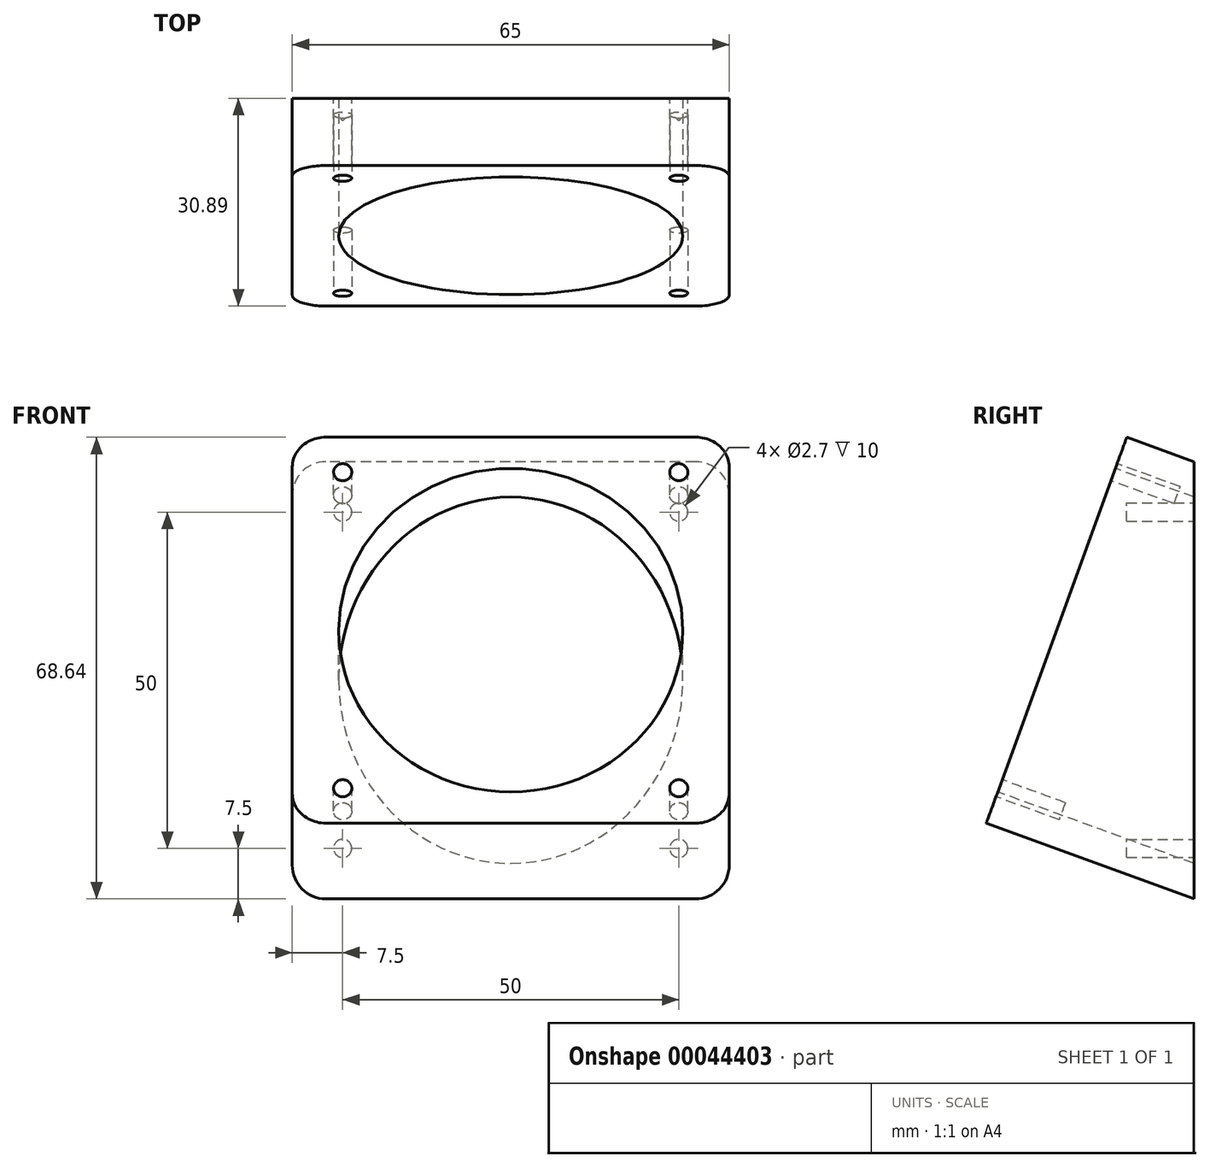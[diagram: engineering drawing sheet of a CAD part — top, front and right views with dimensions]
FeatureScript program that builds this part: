
annotation { "Feature Type Name" : "Feature", "Feature Type Description" : "" }
export const myFeature = defineFeature(function(context is Context, id is Id, definition is map)
    precondition{}
    {
        {
            var Q0;
            Q0=qCreatedBy(makeId("Front.planeOp"),FACE);
            var sketch = newSketch(context, id + "F0", { "sketchPlane" : qUnion([Q0])});
            skLineSegment(sketch, "E0.rect.bottom", {"start": v(27.5, 32.5) * mm, "end": v(-27.5, 32.5) * mm});
            skLineSegment(sketch, "E0.rect.top", {"start": v(27.5, -32.5) * mm, "end": v(-27.5, -32.5) * mm});
            skLineSegment(sketch, "E0.rect.left", {"start": v(32.5, 27.5) * mm, "end": v(32.5, -27.5) * mm});
            skLineSegment(sketch, "E0.rect.right", {"start": v(-32.5, 27.5) * mm, "end": v(-32.5, -27.5) * mm});
            skPoint(sketch, "E0.rect.middle", {"position": v(0, 0) * mm});
            skPoint(sketch, "E1.visualSharp", {"position": v(-32.5, 32.5) * mm});
            skArc(sketch, "E1.filletArc", {"start": v(-27.5, 32.5) * mm, "mid": v(-31.04, 31.04) * mm, "end": v(-32.5, 27.5) * mm});
            skPoint(sketch, "E2.visualSharp", {"position": v(-32.5, -32.5) * mm});
            skArc(sketch, "E2.filletArc", {"start": v(-32.5, -27.5) * mm, "mid": v(-31.04, -31.04) * mm, "end": v(-27.5, -32.5) * mm});
            skPoint(sketch, "E3.visualSharp", {"position": v(32.5, -32.5) * mm});
            skArc(sketch, "E3.filletArc", {"start": v(27.5, -32.5) * mm, "mid": v(31.04, -31.04) * mm, "end": v(32.5, -27.5) * mm});
            skPoint(sketch, "E4.visualSharp", {"position": v(32.5, 32.5) * mm});
            skArc(sketch, "E4.filletArc", {"start": v(32.5, 27.5) * mm, "mid": v(31.04, 31.04) * mm, "end": v(27.5, 32.5) * mm});
            skSolve(sketch);
        }
        {
            var Q0;
            Q0=qCreatedBy(makeId("Front.planeOp"),FACE);
            var sketch = newSketch(context, id + "F1", { "sketchPlane" : qUnion([Q0])});
            skCircle(sketch, "E5", {"center": v(-25, 25) * mm, "radius": 1.35 * mm});
            skCircle(sketch, "E6.MirrorC", {"center": v(25, 25) * mm, "radius": 1.35 * mm});
            skCircle(sketch, "E7.MirrorC", {"center": v(-25, -25) * mm, "radius": 1.35 * mm});
            skCircle(sketch, "E8.MirrorC", {"center": v(25, -25) * mm, "radius": 1.35 * mm});
            skSolve(sketch);
        }
        {
            var Q0;
            Q0=qCreatedBy(makeId("Top.planeOp"),FACE);
            var sketch = newSketch(context, id + "F2", { "sketchPlane" : qUnion([Q0])});
            skLineSegment(sketch, "E9", {"start": v(44.2, -23.15) * mm, "end": v(-58.35, -23.15) * mm, "construction": true});
            skSolve(sketch);
        }
        {
            var Q0;
            Q0=sQuery(id+"F2.wireOp",EDGE,"E9");
            var Q1;
            Q1=qCreatedBy(makeId("Front.planeOp"),FACE);
            cPlane(context, id + "F3", {"entities" : qUnion([Q0, Q1]), "cplaneType" : CPlaneType.LINE_ANGLE, "offset" : 150 * mm, "angle" : 20 * degree, "width" : 150 * mm, "height" : 150 * mm});
        }
        {
            var Q0;
            Q0=qCreatedBy(id+"F3.planeOp",FACE);
            var sketch = newSketch(context, id + "F4", { "sketchPlane" : qUnion([Q0])});
            skLineSegment(sketch, "E10.0", {"start": v(-27.5, 30.54) * mm, "end": v(27.5, 30.54) * mm});
            skLineSegment(sketch, "E10.1", {"start": v(-27.5, -30.54) * mm, "end": v(27.5, -30.54) * mm});
            skLineSegment(sketch, "E10.2", {"start": v(-32.5, 25.84) * mm, "end": v(-32.5, -25.84) * mm});
            skLineSegment(sketch, "E10.3", {"start": v(32.5, 25.84) * mm, "end": v(32.5, -25.84) * mm});
            skPoint(sketch, "E10.4", {"position": v(0, 0) * mm});
            skPoint(sketch, "E10.5", {"position": v(32.5, 30.54) * mm});
            skEllipticalArc(sketch, "E10.6", {});
            skPoint(sketch, "E10.7", {"position": v(32.5, -30.54) * mm});
            skEllipticalArc(sketch, "E10.8", {});
            skPoint(sketch, "E10.9", {"position": v(-32.5, -30.54) * mm});
            skEllipticalArc(sketch, "E10.10", {});
            skPoint(sketch, "E10.11", {"position": v(-32.5, 30.54) * mm});
            skEllipticalArc(sketch, "E10.12", {});
            const initialGuessF4  = {"E10.6": [0.0275, 0.025841547071612483, -1, 0, 0.005, 0.004698463103929543, 3.1415926535897936, 4.71238898038469], "E10.8": [0.0275, -0.025841547071612483, -1, 0, 0.005, 0.004698463103929546, 1.5707963267948963, 3.1415926535897936], "E10.10": [-0.0275, -0.025841547071612483, -1, 0, 0.005, 0.004698463103929546, 0, 1.5707963267948963], "E10.12": [-0.0275, 0.025841547071612486, -1, 0, 0.005, 0.004698463103929539, 4.71238898038469, 0]};
            skSetInitialGuess(sketch, initialGuessF4);
            skSolve(sketch);
        }
        {
            var Q0;
            Q0=makeQuery(id+"F0.imprint","IMPRINT",FACE,{"disambiguationData":[TD([[makeQuery(id+"F0.imprint","IMPRINT",EDGE,{"derivedFrom":sQuery(id+"F0.wireOp",EDGE,"E0.rect.bottom")}),1.0]])]});
            var Q1;
            Q1=makeQuery(id+"F4.imprint","IMPRINT",FACE,{"disambiguationData":[TD([[makeQuery(id+"F4.imprint","IMPRINT",EDGE,{"derivedFrom":sQuery(id+"F4.wireOp",EDGE,"E10.0")}),-1.0]])]});
            loft(context, id + "F5", {"sheetProfilesArray" : [{ "sheetProfileEntities" : qUnion([Q0]) }, { "sheetProfileEntities" : qUnion([Q1]) }]});
        }
        {
            var Q0;
            Q0=qCreatedBy(id+"F3.planeOp",FACE);
            var sketch = newSketch(context, id + "F6", { "sketchPlane" : qUnion([Q0])});
            skCircle(sketch, "E11", {"center": v(-25, 25) * mm, "radius": 1.35 * mm});
            skCircle(sketch, "E12.MirrorC", {"center": v(25, 25) * mm, "radius": 1.35 * mm});
            skCircle(sketch, "E13.MirrorC", {"center": v(-25, -25) * mm, "radius": 1.35 * mm});
            skCircle(sketch, "E14.MirrorC", {"center": v(25, -25) * mm, "radius": 1.35 * mm});
            skSolve(sketch);
        }
        {
            var Q0;
            Q0 = qSketchRegion(id + "F1", true);
            extrude(context, id + "F7", {"entities" : qUnion([Q0]), "operationType" : NewBodyOperationType.REMOVE, "depth" : 10 * mm});
        }
        {
            var Q0;
            Q0 = qSketchRegion(id + "F6", true);
            extrude(context, id + "F8", {"entities" : qUnion([Q0]), "operationType" : NewBodyOperationType.REMOVE, "depth" : 10 * mm});
        }
        {
            var Q0;
            Q0=makeQuery(id+"F5.opLoft","CAP_FACE",FACE,{"disambiguationData":[OSD([makeQuery(id+"F4.imprint","IMPRINT",FACE,{"disambiguationData":[TD([[makeQuery(id+"F4.imprint","IMPRINT",EDGE,{"derivedFrom":sQuery(id+"F4.wireOp",EDGE,"E10.0")}),-1.0]])]})])],"isStart":true});
            var sketch = newSketch(context, id + "F9", { "sketchPlane" : qUnion([Q0])});
            skCircle(sketch, "E15", {"center": v(0, 0) * mm, "radius": 25.6 * mm});
            skLineSegment(sketch, "E16", {"start": v(0, 30.54) * mm, "end": v(0, -30.54) * mm, "construction": true});
            skSolve(sketch);
        }
        {
            var Q0;
            Q0=makeQuery(id+"F9.imprint","IMPRINT",FACE,{"disambiguationData":[TD([[makeQuery(id+"F9.imprint","IMPRINT",EDGE,{"derivedFrom":sQuery(id+"F9.wireOp",EDGE,"E15")}),1.0]])]});
            extrude(context, id + "F10", {"entities" : qUnion([Q0]), "operationType" : NewBodyOperationType.REMOVE, "endBound" : BoundingType.THROUGH_ALL, "oppositeDirection" : true, "depth" : 25 * mm});
        }
    });
